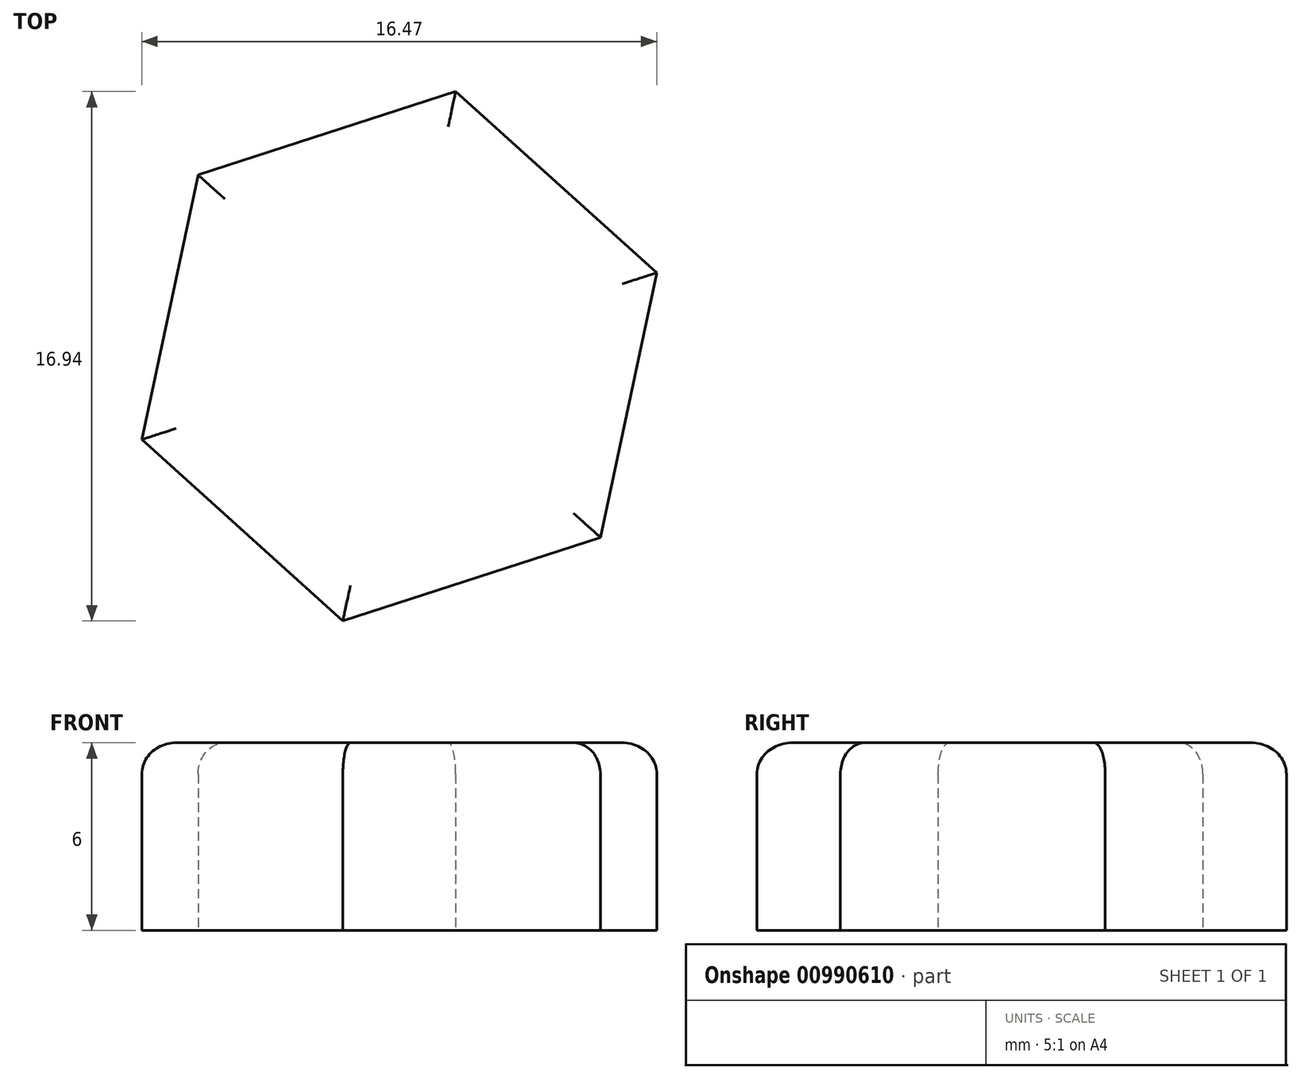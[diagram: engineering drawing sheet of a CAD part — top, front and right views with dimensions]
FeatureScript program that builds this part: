
annotation { "Feature Type Name" : "Feature", "Feature Type Description" : "" }
export const myFeature = defineFeature(function(context is Context, id is Id, definition is map)
    precondition{}
    {
        {
            var Q0;
            Q0=qCreatedBy(makeId("Top.planeOp"),FACE);
            var sketch = newSketch(context, id + "F0", { "sketchPlane" : qUnion([Q0])});
            skCircle(sketch, "E0.cCircle", {"center": v(-12.6, 14.02) * mm, "radius": 7.5 * mm, "construction": true});
            skLineSegment(sketch, "E0.0", {"start": v(-6.17, 8.22) * mm, "end": v(-14.41, 5.55) * mm});
            skLineSegment(sketch, "E0.1", {"start": v(-14.41, 5.55) * mm, "end": v(-20.84, 11.35) * mm});
            skLineSegment(sketch, "E0.2", {"start": v(-20.84, 11.35) * mm, "end": v(-19.04, 19.82) * mm});
            skLineSegment(sketch, "E0.3", {"start": v(-19.04, 19.82) * mm, "end": v(-10.8, 22.5) * mm});
            skLineSegment(sketch, "E0.4", {"start": v(-10.8, 22.5) * mm, "end": v(-4.37, 16.7) * mm});
            skLineSegment(sketch, "E0.5", {"start": v(-4.37, 16.7) * mm, "end": v(-6.17, 8.22) * mm});
            skPoint(sketch, "E0.0.midPoint", {"position": v(-10.3, 6.89) * mm});
            skSolve(sketch);
        }
        {
            var Q0;
            Q0 = qSketchRegion(id + "F0", true);
            extrude(context, id + "F1", {"entities" : qUnion([Q0]), "depth" : 6 * mm, "offsetDistance" : 25 * mm});
        }
        {
            var Q0;
            Q0=makeQuery(id+"F1.opExtrude","CAP_FACE",FACE,{"disambiguationData":[OSD([sQuery(id+"F0.wireOp",EDGE,"E0.0"),sQuery(id+"F0.wireOp",EDGE,"E0.1"),sQuery(id+"F0.wireOp",EDGE,"E0.2"),sQuery(id+"F0.wireOp",EDGE,"E0.3"),sQuery(id+"F0.wireOp",EDGE,"E0.4"),sQuery(id+"F0.wireOp",EDGE,"E0.5")])],"isStart":false});
            fillet(context, id + "F2", {"entities" : qUnion([Q0]), "radius" : 1 * mm, "tangentPropagation" : true, "allowEdgeOverflow" : false});
        }
    });
